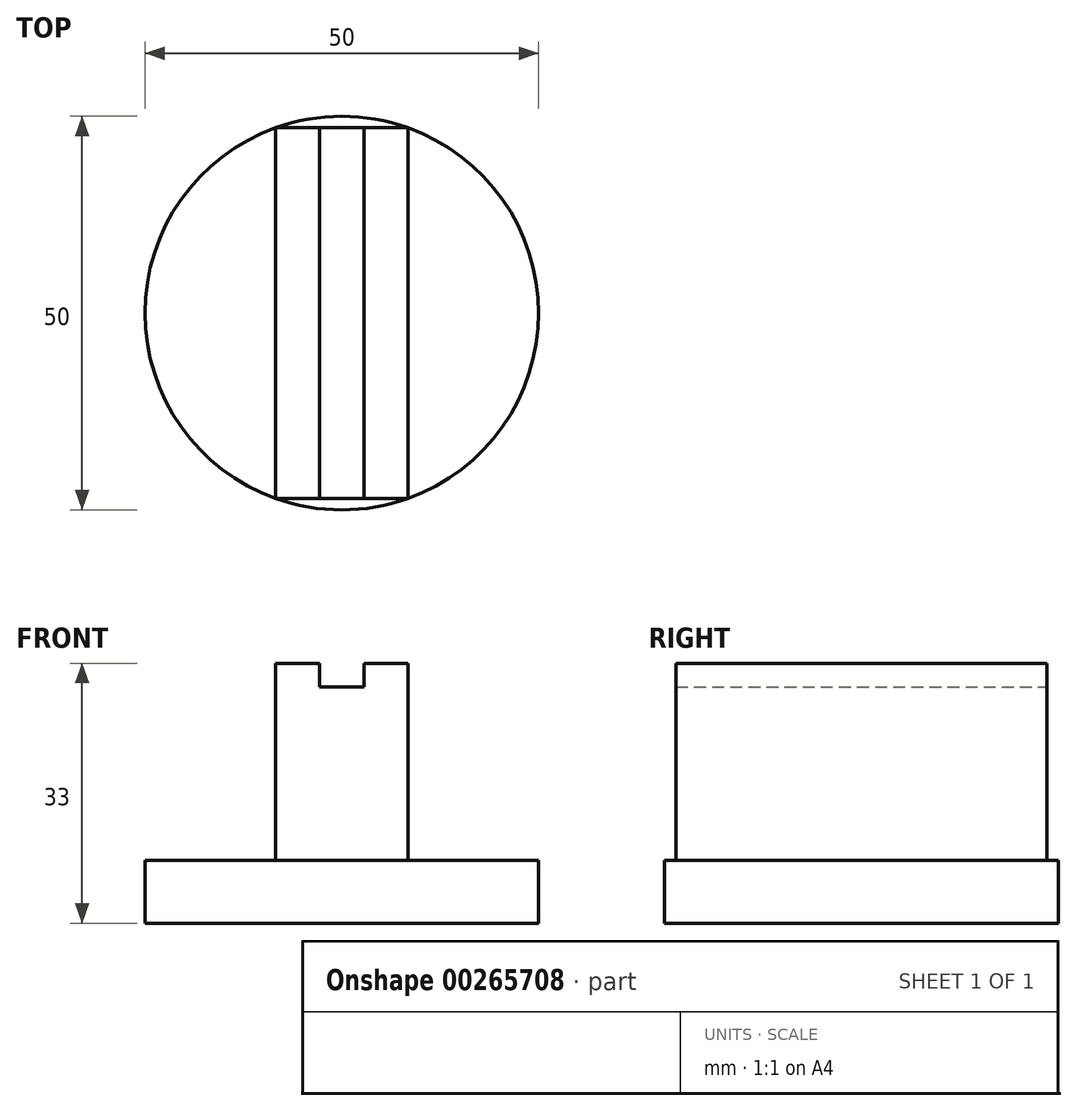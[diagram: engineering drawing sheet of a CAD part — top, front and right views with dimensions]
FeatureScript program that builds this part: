
annotation { "Feature Type Name" : "Feature", "Feature Type Description" : "" }
export const myFeature = defineFeature(function(context is Context, id is Id, definition is map)
    precondition{}
    {
        {
            var Q0;
            Q0=qCreatedBy(makeId("Top.planeOp"),FACE);
            var sketch = newSketch(context, id + "F0", { "sketchPlane" : qUnion([Q0])});
            skCircle(sketch, "E0", {"center": v(0, 0) * mm, "radius": 25 * mm});
            skSolve(sketch);
        }
        {
            var Q0;
            Q0 = qSketchRegion(id + "F0", true);
            extrude(context, id + "F1", {"entities" : qUnion([Q0]), "depth" : 8 * mm});
        }
        {
            var Q0;
            Q0=makeQuery(id+"F1.opExtrude","CAP_FACE",FACE,{"disambiguationData":[OSD([sQuery(id+"F0.wireOp",EDGE,"E0")])],"isStart":false});
            var sketch = newSketch(context, id + "F2", { "sketchPlane" : qUnion([Q0])});
            skLineSegment(sketch, "E1.bottom", {"start": v(-8.4, -23.54) * mm, "end": v(8.4, -23.54) * mm});
            skLineSegment(sketch, "E1.top", {"start": v(-8.4, 23.54) * mm, "end": v(8.4, 23.54) * mm});
            skLineSegment(sketch, "E1.left", {"start": v(-8.4, -23.54) * mm, "end": v(-8.4, 23.54) * mm});
            skLineSegment(sketch, "E1.right", {"start": v(8.4, -23.54) * mm, "end": v(8.4, 23.54) * mm});
            skPoint(sketch, "E1.middle", {"position": v(0, 0) * mm});
            skSolve(sketch);
        }
        {
            var Q0;
            Q0 = qSketchRegion(id + "F2", true);
            extrude(context, id + "F3", {"entities" : qUnion([Q0]), "operationType" : NewBodyOperationType.ADD, "depth" : 25 * mm});
        }
        {
            var Q0;
            Q0=makeQuery(id+"F3.opExtrude","CAP_FACE",FACE,{"disambiguationData":[OSD([sQuery(id+"F2.wireOp",EDGE,"E1.bottom"),sQuery(id+"F2.wireOp",EDGE,"E1.top"),sQuery(id+"F2.wireOp",EDGE,"E1.left"),sQuery(id+"F2.wireOp",EDGE,"E1.right")])],"isStart":false});
            var sketch = newSketch(context, id + "F4", { "sketchPlane" : qUnion([Q0])});
            skLineSegment(sketch, "E2.bottom", {"start": v(-2.85, -23.54) * mm, "end": v(2.85, -23.54) * mm});
            skLineSegment(sketch, "E2.top", {"start": v(-2.85, 23.54) * mm, "end": v(2.85, 23.54) * mm});
            skLineSegment(sketch, "E2.left", {"start": v(-2.85, -23.54) * mm, "end": v(-2.85, 23.54) * mm});
            skLineSegment(sketch, "E2.right", {"start": v(2.85, -23.54) * mm, "end": v(2.85, 23.54) * mm});
            skPoint(sketch, "E2.middle", {"position": v(0, 0) * mm});
            skSolve(sketch);
        }
        {
            var Q0;
            Q0=makeQuery(id+"F4.imprint","IMPRINT",FACE,{"disambiguationData":[TD([[makeQuery(id+"F4.imprint","IMPRINT",EDGE,{"derivedFrom":sQuery(id+"F4.wireOp",EDGE,"E2.bottom")}),1.0]])]});
            extrude(context, id + "F5", {"entities" : qUnion([Q0]), "operationType" : NewBodyOperationType.REMOVE, "oppositeDirection" : true, "depth" : 3 * mm});
        }
    });
